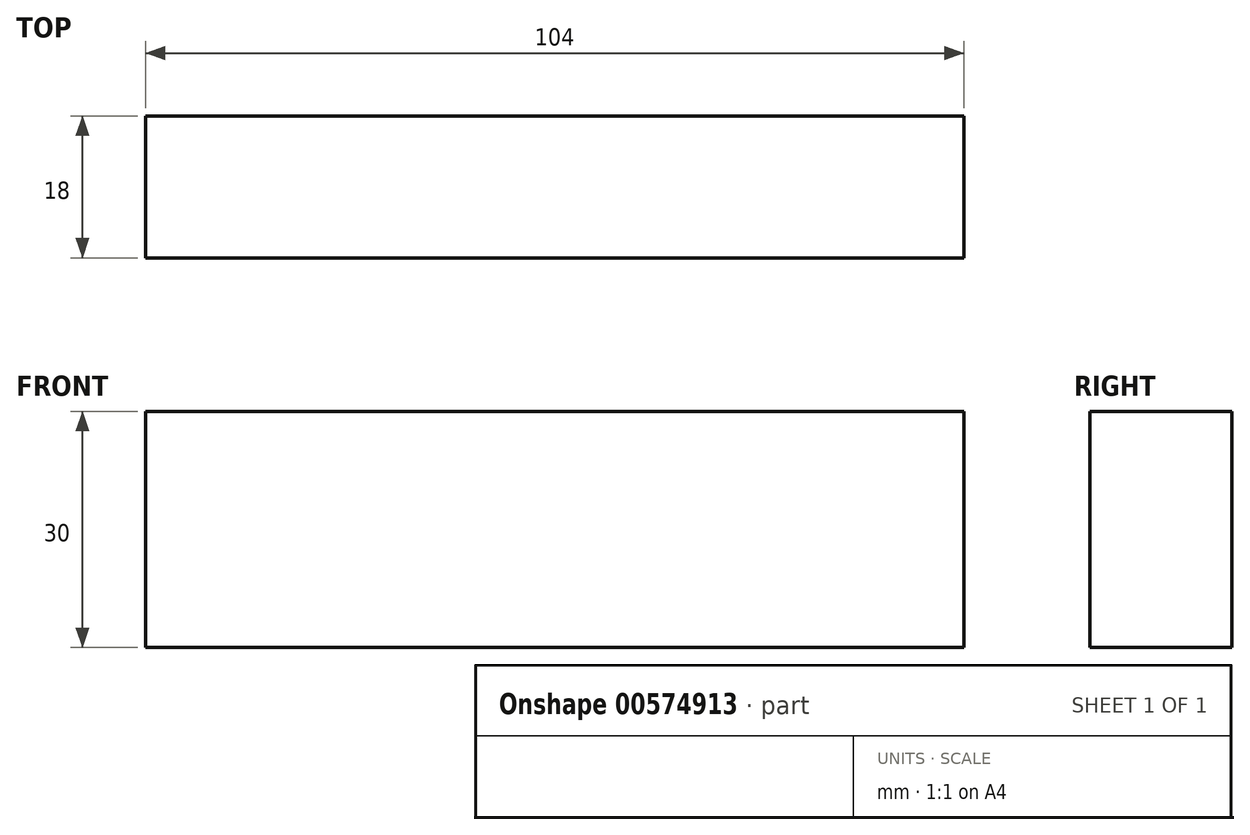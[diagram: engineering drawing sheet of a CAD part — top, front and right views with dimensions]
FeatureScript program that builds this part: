
annotation { "Feature Type Name" : "Feature", "Feature Type Description" : "" }
export const myFeature = defineFeature(function(context is Context, id is Id, definition is map)
    precondition{}
    {
        {
            var Q0;
            Q0=qCreatedBy(makeId("Right.planeOp"),FACE);
            var sketch = newSketch(context, id + "F0", { "sketchPlane" : qUnion([Q0])});
            skLineSegment(sketch, "E0.bottom", {"start": v(-9, 15) * mm, "end": v(9, 15) * mm});
            skLineSegment(sketch, "E0.top", {"start": v(-9, -15) * mm, "end": v(9, -15) * mm});
            skLineSegment(sketch, "E0.left", {"start": v(-9, 15) * mm, "end": v(-9, -15) * mm});
            skLineSegment(sketch, "E0.right", {"start": v(9, 15) * mm, "end": v(9, -15) * mm});
            skPoint(sketch, "E0.middle", {"position": v(0, 0) * mm});
            skSolve(sketch);
        }
        {
            var Q0;
            Q0=makeQuery(id+"F0.imprint","IMPRINT",FACE,{"disambiguationData":[TD([[makeQuery(id+"F0.imprint","IMPRINT",EDGE,{"derivedFrom":sQuery(id+"F0.wireOp",EDGE,"E0.bottom")}),-1.0]])]});
            extrude(context, id + "F1", {"entities" : qUnion([Q0]), "depth" : (140 - 18 - 18) * mm, "offsetDistance" : 25 * mm, "symmetric" : true});
        }
    });
